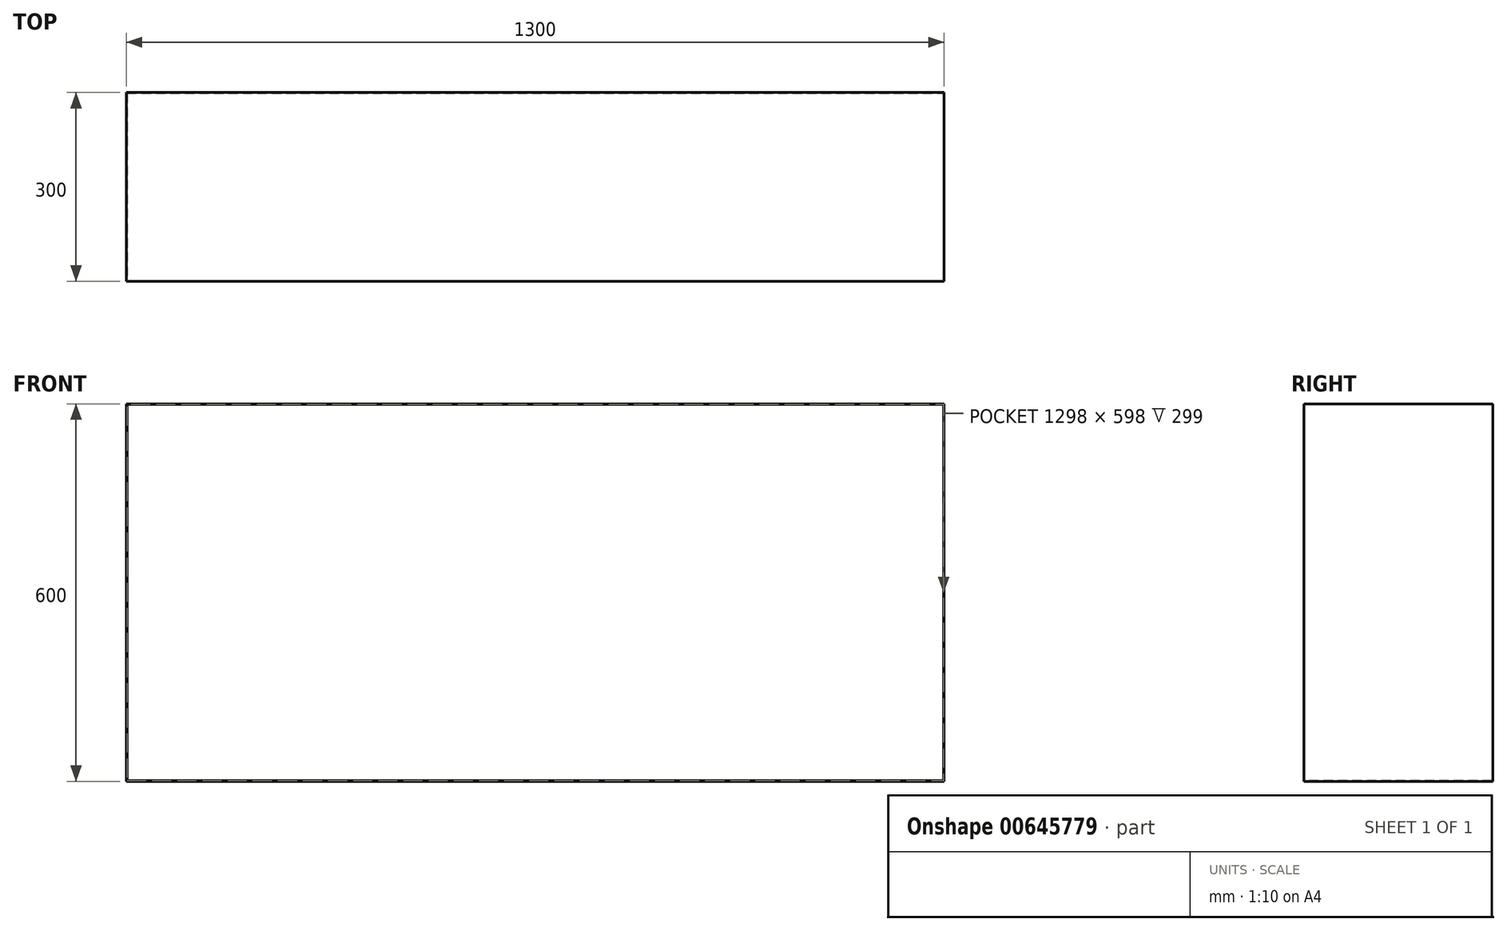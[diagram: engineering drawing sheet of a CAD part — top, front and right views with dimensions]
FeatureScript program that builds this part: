
annotation { "Feature Type Name" : "Feature", "Feature Type Description" : "" }
export const myFeature = defineFeature(function(context is Context, id is Id, definition is map)
    precondition{}
    {
        {
            var Q0;
            Q0=qCreatedBy(makeId("Front.planeOp"),FACE);
            var sketch = newSketch(context, id + "F0", { "sketchPlane" : qUnion([Q0])});
            skLineSegment(sketch, "E0.bottom", {"start": v(0, 0) * mm, "end": v(1300, 0) * mm});
            skLineSegment(sketch, "E0.top", {"start": v(0, 600) * mm, "end": v(1300, 600) * mm});
            skLineSegment(sketch, "E0.left", {"start": v(0, 0) * mm, "end": v(0, 600) * mm});
            skLineSegment(sketch, "E0.right", {"start": v(1300, 0) * mm, "end": v(1300, 600) * mm});
            skSolve(sketch);
        }
        {
            var Q0;
            Q0=makeQuery(id+"F0.imprint","IMPRINT",FACE,{"disambiguationData":[TD([[makeQuery(id+"F0.imprint","IMPRINT",EDGE,{"derivedFrom":sQuery(id+"F0.wireOp",EDGE,"E0.bottom")}),1.0]])]});
            extrude(context, id + "F1", {"entities" : qUnion([Q0]), "depth" : 300 * mm, "offsetDistance" : 25 * mm});
        }
        {
            var Q0;
            Q0=makeQuery(id+"F1.opExtrude","CAP_FACE",FACE,{"disambiguationData":[OSD([sQuery(id+"F0.wireOp",EDGE,"E0.bottom"),sQuery(id+"F0.wireOp",EDGE,"E0.top"),sQuery(id+"F0.wireOp",EDGE,"E0.left"),sQuery(id+"F0.wireOp",EDGE,"E0.right")])],"isStart":false});
            var sketch = newSketch(context, id + "F2", { "sketchPlane" : qUnion([Q0])});
            skLineSegment(sketch, "E1.bottom", {"start": v(1, 599) * mm, "end": v(1299, 599) * mm});
            skLineSegment(sketch, "E1.top", {"start": v(1, 1) * mm, "end": v(1299, 1) * mm});
            skLineSegment(sketch, "E1.left", {"start": v(1, 599) * mm, "end": v(1, 1) * mm});
            skLineSegment(sketch, "E1.right", {"start": v(1299, 599) * mm, "end": v(1299, 1) * mm});
            skSolve(sketch);
        }
        {
            var Q0;
            Q0=qSketchRegion(id+"F2",true);
            extrude(context, id + "F3", {"entities" : qUnion([Q0]), "operationType" : NewBodyOperationType.REMOVE, "oppositeDirection" : true, "depth" : 299 * mm, "offsetDistance" : 25 * mm});
        }
    });
